# Revit family: Faucet-Lavatory-KOHLER-ALEO-K-98868T_1
name_source: partatom
category: Plumbing Fixtures
revit_build: Autodesk Revit 2017 (Build: 20160225_1515(x64)
units: mm (PartAtom-declared; Revit-internal decimal feet)

## family parameters
Cut with Voids When Loaded = No
Host = Face
OmniClass Number = 23.31.11.00
OmniClass Title = Faucets
Part Type = Normal
Room Calculation Point = No
Round Connector Dimension = Use Diameter
Shared = No

## types (5) — shared parameters
ADA Compliant = No
Assembly Code = D2010
CW Connection = Yes
Cold Water Inlet = Cold Water Inlet
Date Modified = 12/27/2021
Default Elevation = 36"
Drain Included = Yes
HW Connection = Yes
Handle Clearance = 3 1/2"
Height = 12 11/16"
Hot Water Inlet = Hot Water Inlet
Length = 6 1/4"
Manufacturer = KOHLER Co.
Master Format 2014 = 22 41 39
Master Format 2014 Name = Residential Faucets, Supplies, and Trim
Material = Premium Metal Construction
Product Name = ALEO
Spout Reach = 6 1/4"
URL = http://www.kohler.com.cn
Vent Connection = No
Waste Connection = No
Waste Water Outlet = Waste Water Outlet
WaterSense Certified = No
Width = 2"

## per-type parameters (varying)
| type | Description | Finish | Flow Rate | Lift Rod | Model | Plug Screw Finish | Pressure | Product Documentation Link | Product Page URL | Type |
| 2.2 GPM, With Lift Rod, CP-Polished Chrome | Single lever bowl mixer | Kohler-Metal-CP-Polished_Chrome | 2 GPM | Yes | K-98868T-4-CP | Kohler-Plastic-58-Thunder_Grey | 60.00 psi | https://files.kohler.com.cn | https://www.kohler.com.cn | 1 |
| 2.2 GPM, With Lift Rod, BL-Matte Black | Single lever bowl mixer | Kohler-Metal-BL-Matte_Black | 2 GPM | Yes | K-98868T-4-BL | Kohler-Plastic-7-Black_Black | 60.00 psi | https://files.kohler.com.cn | https://www.kohler.com.cn | 2 |
| 2.2 GPM, Without Lift Rod, CP-Polished Chrome | Single Handle Tall Lavatory Faucet | Kohler-Metal-CP-Polished_Chrome | 2 GPM | No | K-98868T-B4-CP | Kohler-Plastic-58-Thunder_Grey | 45.00 psi |  |  | 3 |
| 2.2 GPM, Without Lift Rod, BL-Matte Black | Single Handle Tall Lavatory Faucet | Kohler-Metal-BL-Matte_Black | 2 GPM | No | K-98868T-B4-BL | Kohler-Plastic-7-Black_Black | 45.00 psi |  |  | 4 |
| 1.2 GPM, Without Lift Rod, CP-Polished Chrome | Single Handle Tall Lavatory Faucet | Kohler-Metal-CP-Polished_Chrome | 1 GPM | No | K-98868T-B4E2-CP | Kohler-Plastic-58-Thunder_Grey | 45.00 psi |  |  | 5 |

## geometry (parser evidence)
native form markers: Sweep x5
no freeform markers — native parametric forms only
